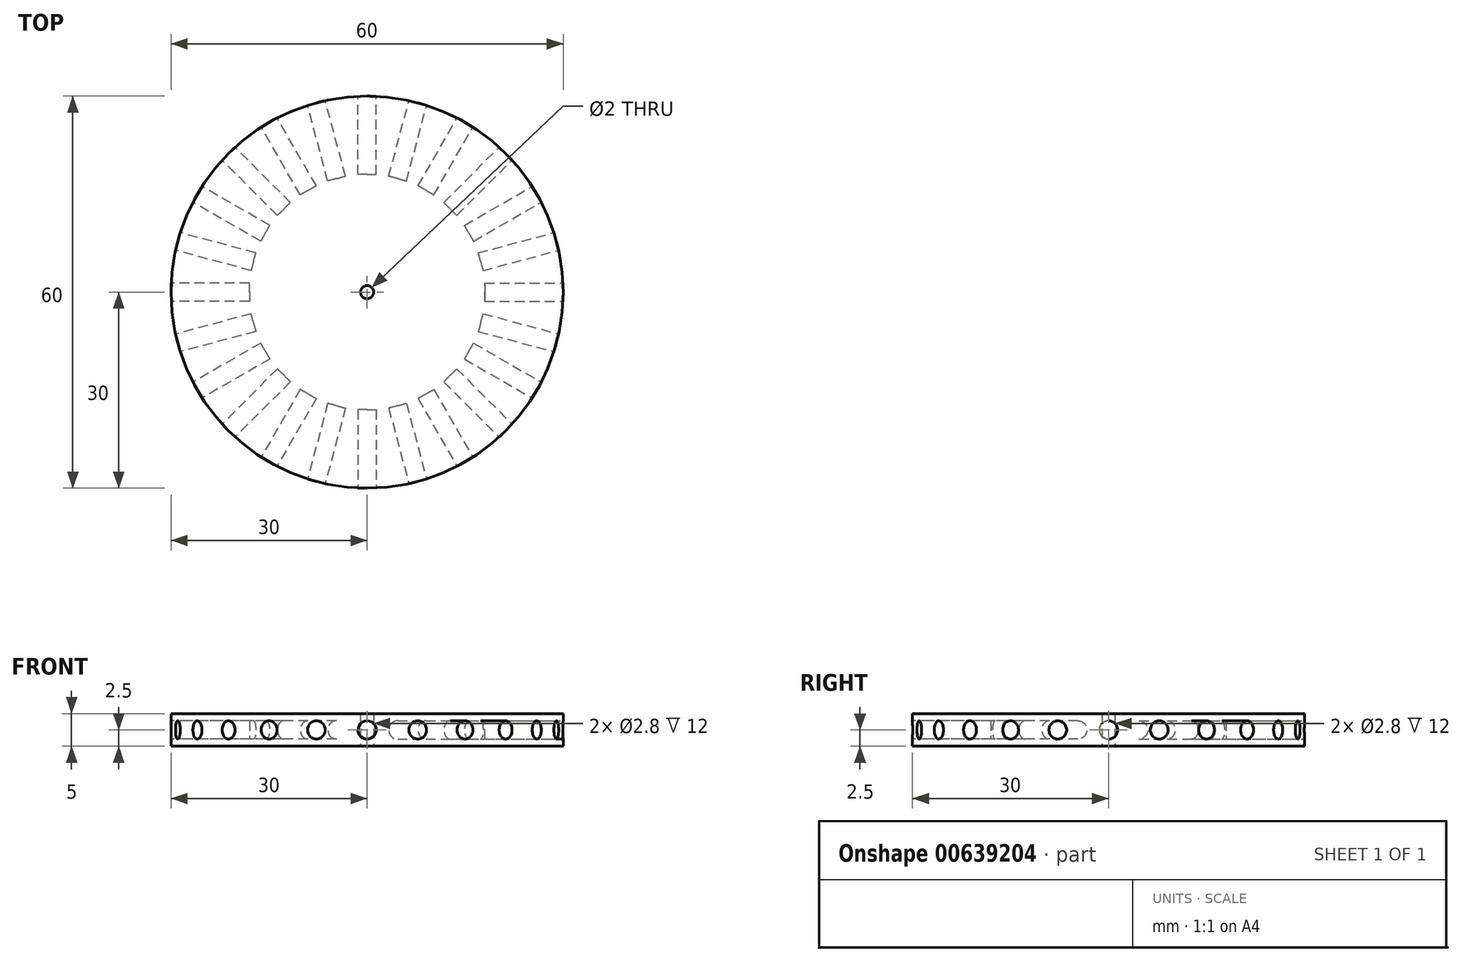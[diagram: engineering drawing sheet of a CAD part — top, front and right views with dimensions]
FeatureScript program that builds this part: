
annotation { "Feature Type Name" : "Feature", "Feature Type Description" : "" }
export const myFeature = defineFeature(function(context is Context, id is Id, definition is map)
    precondition{}
    {
        {
            var Q0;
            Q0=qCreatedBy(makeId("Top.planeOp"),FACE);
            var sketch = newSketch(context, id + "F0", { "sketchPlane" : qUnion([Q0])});
            skCircle(sketch, "E0", {"center": v(0, 0) * mm, "radius": 1 * mm});
            skCircle(sketch, "E1", {"center": v(0, 0) * mm, "radius": 30 * mm});
            skSolve(sketch);
        }
        {
            var Q0;
            Q0=qSketchRegion(id+"F0",true);
            extrude(context, id + "F1", {"entities" : qUnion([Q0]), "depth" : 5 * mm, "offsetDistance" : 25 * mm});
        }
        {
            var Q0;
            Q0=qCreatedBy(makeId("Front.planeOp"),FACE);
            cPlane(context, id + "F2", {"entities" : qUnion([Q0]), "cplaneType" : CPlaneType.OFFSET, "offset" : 30 * mm, "oppositeDirection" : true, "width" : 150 * mm, "height" : 150 * mm});
        }
        {
            var Q0;
            Q0=qCreatedBy(id+"F2.planeOp",FACE);
            var sketch = newSketch(context, id + "F3", { "sketchPlane" : qUnion([Q0])});
            skCircle(sketch, "E2", {"center": v(0, 2.5) * mm, "radius": 1.4 * mm});
            skLineSegment(sketch, "E3.0", {"start": v(-30, 5) * mm, "end": v(30, 5) * mm, "construction": true});
            skLineSegment(sketch, "E4.0", {"start": v(-30, 0) * mm, "end": v(30, 0) * mm, "construction": true});
            skLineSegment(sketch, "E5", {"start": v(0, 0) * mm, "end": v(0, 5) * mm, "construction": true});
            skSolve(sketch);
        }
        {
            var Q0;
            Q0 = qSketchRegion(id + "F3", true);
            extrude(context, id + "F4", {"entities" : qUnion([Q0]), "depth" : 12 * mm, "offsetDistance" : 25 * mm});
        }
        {
            var Q0;
            Q0=makeQuery(id+"F4.opExtrude","SWEPT_BODY",BODY,{"disambiguationData":[OSD([sQuery(id+"F3.wireOp",EDGE,"E2")])]});
            var Q1;
            Q1=makeQuery(id+"F1.opExtrude","CAP_EDGE",EDGE,{"disambiguationData":[OSD([sQuery(id+"F0.wireOp",EDGE,"E0")])],"isStart":false});
            circularPattern(context, id + "F5", {"operationType" : NewBodyOperationType.REMOVE, "entities" : qUnion([Q0]), "axis" : qUnion([Q1]), "angle" : 360 * degree, "instanceCount" : 24, "equalSpace" : true});
        }
    });
